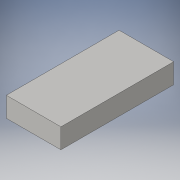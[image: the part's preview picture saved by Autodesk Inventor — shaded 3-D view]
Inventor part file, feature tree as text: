
AUTODESK INVENTOR PART (.ipt)
format: ipt  version: 2016 (Build 200138000, 138)  size: 83,968 bytes
history: native  units: in
note: dims shown in document units (in); Inventor stores cm internally (conversion verified against a paired STEP export)
features: extrude x1, sketch x1
ambient origin geometry x8: Origin, YZ Plane, XZ Plane, XY Plane, X Axis, Y Axis, Z Axis, Center Point
bodies: Solid1 (feature_tree)
feature tree (2):
  extrude  "Extrusion1"  Depth=2.7402in
  sketch  "Sketch1"  dims[d0=1.3268in d1=2.7402in d2=0.4843in d3=0.0in]
